# Revit family: 2102A_HBA_WASP
name_source: partatom
category: Communication Devices
units: mm (PartAtom-declared; Revit-internal decimal feet)

## family parameters
Cut with Voids When Loaded = No
Host = Face
Maintain Annotation Orientation = No
OmniClass Number = 23.85.80.11.27
OmniClass Title = Lighting Controls
Part Type = Normal
Room Calculation Point = No
Round Connector Dimension = Use Diameter
Shared = Yes

## types (1)
- 2102A_HBA_WASP
    Assembly Code = D5090
    Certifications = Conforms to UL STD 508, UL STD 244A
LWO version conforms to IP65
    Coverage = 360°, 180°, Aisle, Half Aisle
    Default Elevation = 48 "
    Description = The Dimming WASP Indoor/Outdoor Occupancy Sensor is
specifically designed to provide 0-10V (Class 1) control of
dimmable fixtures. Easy to use dip switches allow the user to
set unoccupied and occupied dimming levels. The sensor is
available in end mount and surface mount versions in both
line and low voltage options. Interchangeable twist-on lenses
eliminate need for field masking. All Dimming WASP sensors
feature a daylight sensor for On/Off control of fixtures when
there is sufficient natural light.
    Features = Digital Passive Infrared (PIR) sensor 
Supported mounting heights: 
High mount lens: 30 ft (9.14m) outdoors; 45 ft (13.72m) indoors
Low mount lens: 16 ft (4.88m) indoors/outdoors 
Controls 0-10V dimmable ballasts 
User controlled dimming presets 
Daylight sensor for daylight harvesting applications 
End mount and surface mount versions 
Interchangeable high/low area detection lens options 
Low voltage and line voltage models available 
Low temperature/water-tight/indoor-outdoor versions 
Withstands low temperature and conforms to IP65 water-tight standards 
UL and cUL listed
Five-year limited warranty
    Housing Material = Paint -  Matte White
    Manufacturer = NX Lighting Controls
    Model = Dimming WASP
    Power Requirements = Line Voltage sensors: 120/277/347VAC, 208/240VAC, 480VAC, 60 Hz
Low Voltage sensors: 24VDC (uses UVPP or MP-Series power pack – not included)
    Sensing Element = Glass -  White
    Type Comments = Occupancy Sensors and Controllers
    URL = https://www.currentlighting.com
    Warranty = 5-Years Warranty
    Width = 4 "

## geometry (parser evidence)
native form markers: Sweep x3
no freeform markers — native parametric forms only
